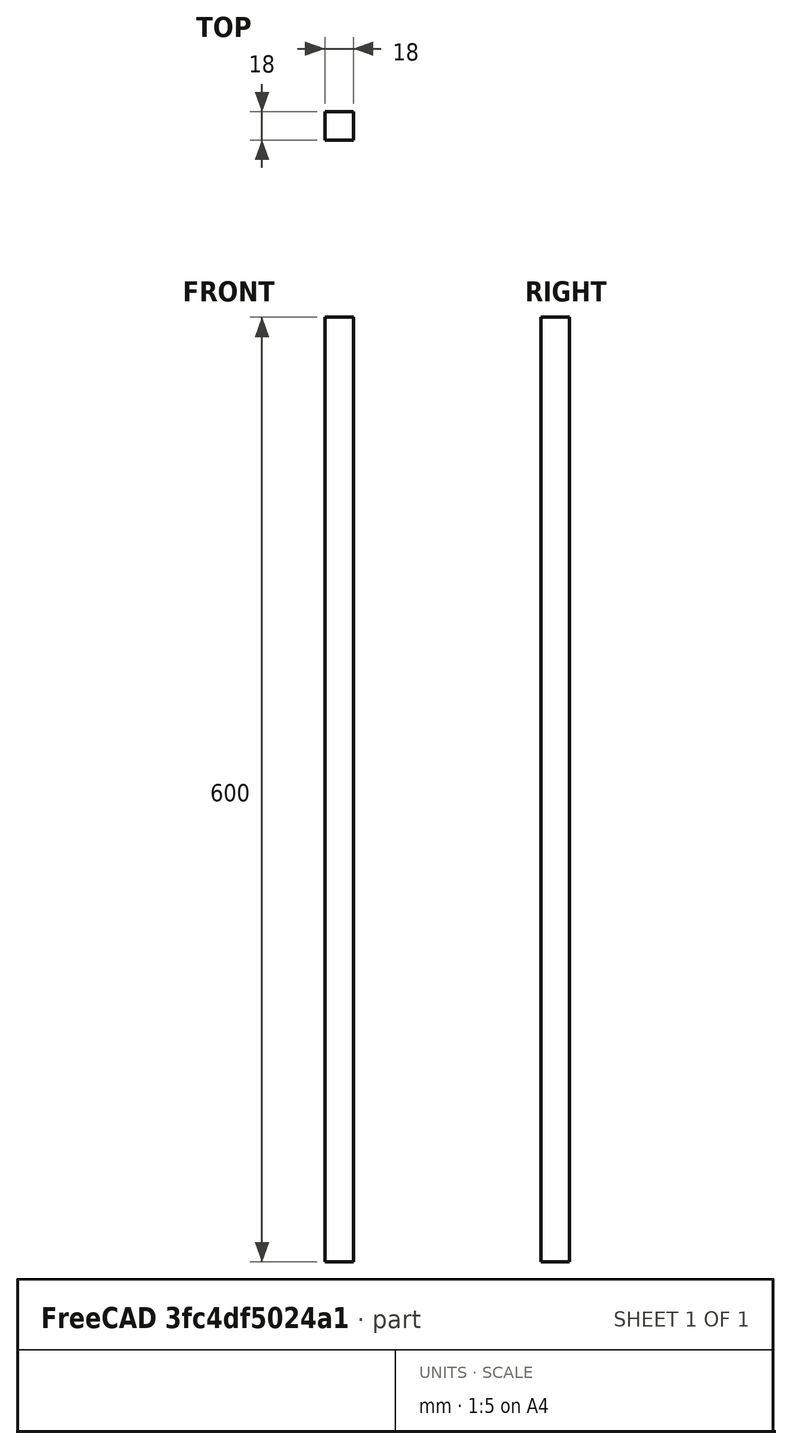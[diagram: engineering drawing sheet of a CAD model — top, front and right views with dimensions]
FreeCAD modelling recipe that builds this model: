
FCSTD DOCUMENT  (FreeCAD 0.20R29603 (Git))
Label: 3000_Z_strut_x_18_18_530
License: All rights reserved
LicenseURL: http://en.wikipedia.org/wiki/All_rights_reserved
objects: Sketcher::SketchObject×1, PartDesign::Pad×1, PartDesign::Body×1
note: 4 computed .brp shape members not serialized (recipe doc carries the construction recipe); baked Part::Feature solids carry a one-line shape summary decoded from their .brp

FEATURE [Sketcher::SketchObject] Sketch
  FullyConstrained = true
  MapMode = 5
  Support = -> [XY_Plane]
  sketch-geometry (4):
    g0: LineSegment StartX=0 StartY=0 StartZ=0 EndX=18 EndY=0 EndZ=0
    g1: LineSegment StartX=18 StartY=0 StartZ=0 EndX=18 EndY=18 EndZ=0
    g2: LineSegment StartX=18 StartY=18 StartZ=0 EndX=0 EndY=18 EndZ=0
    g3: LineSegment StartX=0 StartY=18 StartZ=0 EndX=0 EndY=0 EndZ=0
  constraints (11):
    c: Coincident(g0,g1)
    c: Coincident(g1,g2)
    c: Coincident(g2,g3)
    c: Coincident(g3,g0)
    c: Horizontal(g0)
    c: Horizontal(g2)
    c: Vertical(g1)
    c: Vertical(g3)
    c: Coincident(g0,g-1)
    c: DistanceX(g2,g2) = 18
    c: DistanceY(g1,g1) = 18
FEATURE [PartDesign::Pad] Pad
  Direction = (0,0,1)
  Length = 600
  Length2 = 100
  Profile = -> Sketch
  ReferenceAxis = -> Sketch [N_Axis]
  Type = 0
FEATURE [PartDesign::Body] Body
  Group = -> [Sketch,Pad]
  Origin = -> Origin
  Tip = -> Pad
